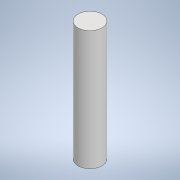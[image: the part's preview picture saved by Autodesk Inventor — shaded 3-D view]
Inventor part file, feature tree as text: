
AUTODESK INVENTOR PART (.ipt)
format: ipt  version: 2020 (Build 240168000, 168)  size: 90,112 bytes
history: native  units: mm
features: extrude x1, sketch x1
ambient origin geometry x8: Origin, YZ Plane, XZ Plane, XY Plane, X Axis, Y Axis, Z Axis, Center Point
bodies: Solid1 (feature_tree)
feature tree (2):
  extrude  "Extrusion1"  Depth=10.0mm TaperAngle=0.0deg
  sketch  "Sketch1"  dims[d0=3.0mm d1=10.0mm d2=0.0mm]
